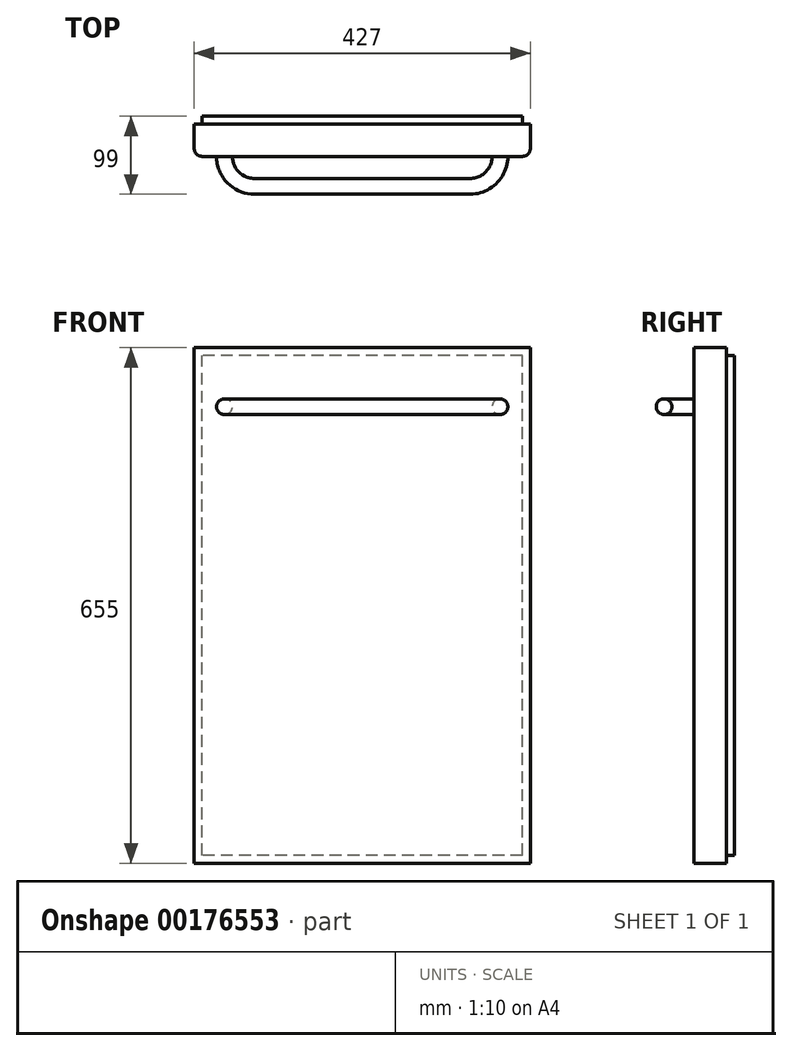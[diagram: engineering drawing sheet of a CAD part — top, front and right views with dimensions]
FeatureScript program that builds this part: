
annotation { "Feature Type Name" : "Feature", "Feature Type Description" : "" }
export const myFeature = defineFeature(function(context is Context, id is Id, definition is map)
    precondition{}
    {
        {
            var Q0;
            Q0=qCreatedBy(makeId("Front.planeOp"),FACE);
            var sketch = newSketch(context, id + "F0", { "sketchPlane" : qUnion([Q0])});
            skLineSegment(sketch, "E0.bottom", {"start": v(213.5, 327.5) * mm, "end": v(-213.5, 327.5) * mm});
            skLineSegment(sketch, "E0.top", {"start": v(213.5, -327.5) * mm, "end": v(-213.5, -327.5) * mm});
            skLineSegment(sketch, "E0.left", {"start": v(213.5, 327.5) * mm, "end": v(213.5, -327.5) * mm});
            skLineSegment(sketch, "E0.right", {"start": v(-213.5, 327.5) * mm, "end": v(-213.5, -327.5) * mm});
            skPoint(sketch, "E0.middle", {"position": v(0, 0) * mm});
            skSolve(sketch);
        }
        {
            var Q0;
            Q0 = qSketchRegion(id + "F0", true);
            extrude(context, id + "F1", {"entities" : qUnion([Q0]), "depth" : 41 * mm});
        }
        {
            var Q0;
            Q0=makeQuery(id+"F1.opExtrude","CAP_EDGE",EDGE,{"disambiguationData":[OSD([sQuery(id+"F0.wireOp",EDGE,"E0.right")])],"isStart":false});
            var Q1;
            Q1=makeQuery(id+"F1.opExtrude","CAP_EDGE",EDGE,{"disambiguationData":[OSD([sQuery(id+"F0.wireOp",EDGE,"E0.left")])],"isStart":false});
            fillet(context, id + "F2", {"entities" : qUnion([Q0, Q1]), "radius" : 10 * mm, "tangentPropagation" : true, "allowEdgeOverflow" : false});
        }
        {
            var Q0;
            Q0=makeQuery(id+"F1.opExtrude","CAP_FACE",FACE,{"disambiguationData":[OSD([sQuery(id+"F0.wireOp",EDGE,"E0.bottom"),sQuery(id+"F0.wireOp",EDGE,"E0.top"),sQuery(id+"F0.wireOp",EDGE,"E0.left"),sQuery(id+"F0.wireOp",EDGE,"E0.right")])],"isStart":true});
            var sketch = newSketch(context, id + "F3", { "sketchPlane" : qUnion([Q0])});
            skLineSegment(sketch, "E1.bottom", {"start": v(-203.5, -317.5) * mm, "end": v(203.5, -317.5) * mm});
            skLineSegment(sketch, "E1.top", {"start": v(-203.5, 317.5) * mm, "end": v(203.5, 317.5) * mm});
            skLineSegment(sketch, "E1.left", {"start": v(-203.5, -317.5) * mm, "end": v(-203.5, 317.5) * mm});
            skLineSegment(sketch, "E1.right", {"start": v(203.5, -317.5) * mm, "end": v(203.5, 317.5) * mm});
            skSolve(sketch);
        }
        {
            var Q0;
            Q0 = qSketchRegion(id + "F3", true);
            extrude(context, id + "F4", {"entities" : qUnion([Q0]), "depth" : 10 * mm});
        }
        {
            var Q0;
            Q0=makeQuery(id+"F1.opExtrude","SWEPT_FACE",FACE,{"disambiguationData":[OSD([sQuery(id+"F0.wireOp",EDGE,"E0.bottom")])]});
            cPlane(context, id + "F5", {"entities" : qUnion([Q0]), "cplaneType" : CPlaneType.OFFSET, "offset" : 75 * mm, "oppositeDirection" : true, "width" : 150 * mm, "height" : 150 * mm});
        }
        {
            var Q0;
            Q0=qCreatedBy(id+"F5.planeOp",FACE);
            var sketch = newSketch(context, id + "F6", { "sketchPlane" : qUnion([Q0])});
            skLineSegment(sketch, "E2", {"start": v(-175, -41) * mm, "end": v(-175, -41) * mm});
            skLineSegment(sketch, "E3", {"start": v(-137, -79) * mm, "end": v(137, -79) * mm});
            skLineSegment(sketch, "E4", {"start": v(175, -41) * mm, "end": v(175, -41) * mm});
            skPoint(sketch, "E5.visualSharp", {"position": v(-175, -79) * mm});
            skArc(sketch, "E5.filletArc", {"start": v(-175, -41) * mm, "mid": v(-163.87, -67.87) * mm, "end": v(-137, -79) * mm});
            skPoint(sketch, "E6.visualSharp", {"position": v(175, -79) * mm});
            skArc(sketch, "E6.filletArc", {"start": v(137, -79) * mm, "mid": v(163.87, -67.87) * mm, "end": v(175, -41) * mm});
            skSolve(sketch);
        }
        {
            var Q0;
            Q0=makeQuery(id+"F1.opExtrude","CAP_FACE",FACE,{"disambiguationData":[OSD([sQuery(id+"F0.wireOp",EDGE,"E0.bottom"),sQuery(id+"F0.wireOp",EDGE,"E0.top"),sQuery(id+"F0.wireOp",EDGE,"E0.left"),sQuery(id+"F0.wireOp",EDGE,"E0.right")])],"isStart":false});
            var sketch = newSketch(context, id + "F7", { "sketchPlane" : qUnion([Q0])});
            skCircle(sketch, "E7", {"center": v(-175, 252.5) * mm, "radius": 10 * mm});
            skSolve(sketch);
        }
        {
            var Q0;
            Q0=makeQuery(id+"F7.imprint","IMPRINT",FACE,{"disambiguationData":[TD([[makeQuery(id+"F7.imprint","IMPRINT",EDGE,{"derivedFrom":sQuery(id+"F7.wireOp",EDGE,"E7")}),1.0]])]});
            var Q1;
            Q1=sQuery(id+"F6.wireOp",EDGE,"E5.filletArc");
            var Q2;
            Q2=sQuery(id+"F6.wireOp",EDGE,"E3");
            var Q3;
            Q3=sQuery(id+"F6.wireOp",EDGE,"E6.filletArc");
            sweep(context, id + "F8", {"operationType" : NewBodyOperationType.ADD, "profiles" : qUnion([Q0]), "path" : qUnion([Q1, Q2, Q3])});
        }
    });
